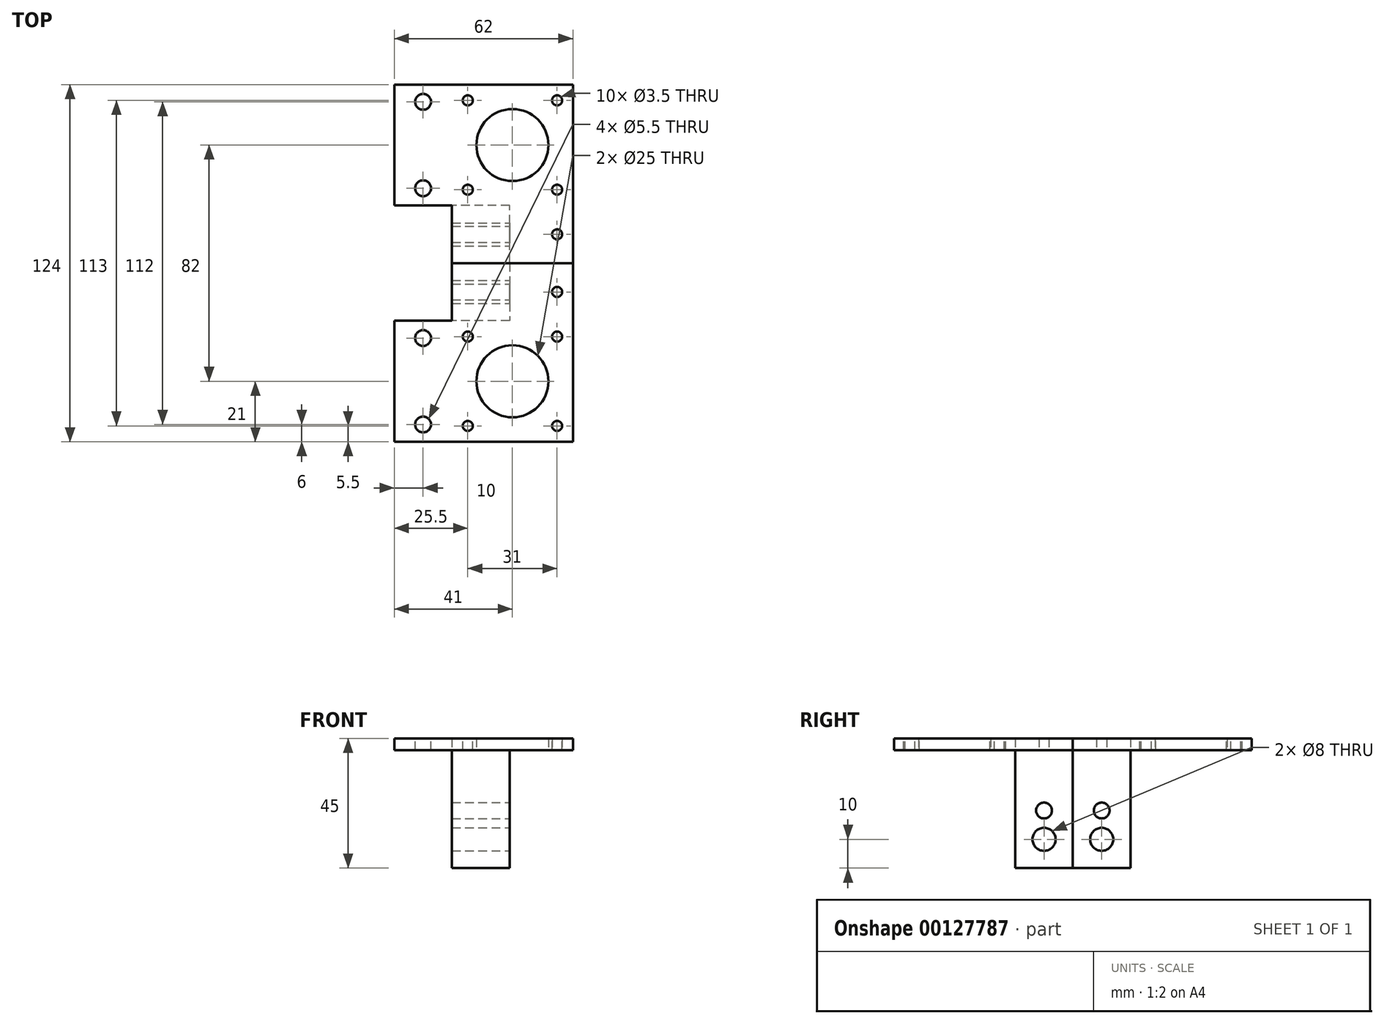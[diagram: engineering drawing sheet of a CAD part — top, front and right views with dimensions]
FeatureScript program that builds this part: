
annotation { "Feature Type Name" : "Feature", "Feature Type Description" : "" }
export const myFeature = defineFeature(function(context is Context, id is Id, definition is map)
    precondition{}
    {
        {
            var Q0;
            Q0=qCreatedBy(makeId("Top.planeOp"),FACE);
            var sketch = newSketch(context, id + "F0", { "sketchPlane" : qUnion([Q0])});
            skLineSegment(sketch, "E0.bottom", {"start": v(21, -21) * mm, "end": v(-21, -21) * mm});
            skLineSegment(sketch, "E0.top", {"start": v(21, 21) * mm, "end": v(-21, 21) * mm});
            skLineSegment(sketch, "E0.left", {"start": v(21, -21) * mm, "end": v(21, 21) * mm});
            skLineSegment(sketch, "E0.right", {"start": v(-21, -21) * mm, "end": v(-21, 21) * mm});
            skPoint(sketch, "E0.middle", {"position": v(0, 0) * mm});
            skSolve(sketch);
        }
        {
            var Q0;
            Q0=makeQuery(id+"F0.imprint","IMPRINT",FACE,{"disambiguationData":[TD([[makeQuery(id+"F0.imprint","IMPRINT",EDGE,{"derivedFrom":sQuery(id+"F0.wireOp",EDGE,"E0.bottom")}),-1.0]])]});
            extrude(context, id + "F1", {"entities" : qUnion([Q0]), "endBound" : BoundingType.SYMMETRIC, "depth" : 4 * mm});
        }
        {
            var Q0;
            Q0=makeQuery(id+"F1.opExtrude","CAP_FACE",FACE,{"disambiguationData":[OSD([sQuery(id+"F0.wireOp",EDGE,"E0.bottom"),sQuery(id+"F0.wireOp",EDGE,"E0.top"),sQuery(id+"F0.wireOp",EDGE,"E0.left"),sQuery(id+"F0.wireOp",EDGE,"E0.right")])],"isStart":false});
            var sketch = newSketch(context, id + "F2", { "sketchPlane" : qUnion([Q0])});
            skCircle(sketch, "E1", {"center": v(-15.5, 15.5) * mm, "radius": 1.75 * mm});
            skLineSegment(sketch, "E2", {"start": v(-12.66, 0) * mm, "end": v(0, 0) * mm, "construction": true});
            skLineSegment(sketch, "E3", {"start": v(0, 0) * mm, "end": v(0, 15.8) * mm, "construction": true});
            skCircle(sketch, "E4.MirrorC", {"center": v(15.5, 15.5) * mm, "radius": 1.75 * mm});
            skCircle(sketch, "E5.MirrorC", {"center": v(-15.5, -15.5) * mm, "radius": 1.75 * mm});
            skCircle(sketch, "E6.MirrorC", {"center": v(15.5, -15.5) * mm, "radius": 1.75 * mm});
            skSolve(sketch);
        }
        {
            var Q0;
            Q0=qSketchRegion(id+"F2",true);
            extrude(context, id + "F3", {"entities" : qUnion([Q0]), "operationType" : NewBodyOperationType.REMOVE, "endBound" : BoundingType.THROUGH_ALL, "oppositeDirection" : true, "depth" : 25 * mm});
        }
        {
            var Q0;
            Q0=makeQuery(id+"F1.opExtrude","SWEPT_FACE",FACE,{"disambiguationData":[OSD([sQuery(id+"F0.wireOp",EDGE,"E0.right")])]});
            extrude(context, id + "F4", {"entities" : qUnion([Q0]), "operationType" : NewBodyOperationType.ADD, "depth" : 20 * mm});
        }
        {
            var Q0;
            {var subQ0=sQuery(id+"F0.wireOp",EDGE,"E0.right");Q0=makeQuery(id+"F4.boolean.opBoolean","MERGE",FACE,{"derivedFrom":[makeQuery(id+"F1.opExtrude","CAP_FACE",FACE,{"disambiguationData":[OSD([sQuery(id+"F0.wireOp",EDGE,"E0.bottom"),sQuery(id+"F0.wireOp",EDGE,"E0.top"),sQuery(id+"F0.wireOp",EDGE,"E0.left"),subQ0])],"isStart":false}),makeQuery(id+"F4.opExtrude","SWEPT_FACE",FACE,{"disambiguationData":[OSD([subQ0]),TDD([makeQuery(id+"F1.opExtrude","CAP_EDGE",EDGE,{"disambiguationData":[OSD([subQ0])],"isStart":false})])]})]});}
            var sketch = newSketch(context, id + "F5", { "sketchPlane" : qUnion([Q0])});
            skLineSegment(sketch, "E7", {"start": v(0, 0) * mm, "end": v(-48.41, 0) * mm, "construction": true});
            skCircle(sketch, "E8", {"center": v(-31, 15) * mm, "radius": 2.75 * mm});
            skCircle(sketch, "E9.MirrorC", {"center": v(-31, -15) * mm, "radius": 2.75 * mm});
            skSolve(sketch);
        }
        {
            var Q0;
            Q0=qSketchRegion(id+"F5",true);
            extrude(context, id + "F6", {"entities" : qUnion([Q0]), "operationType" : NewBodyOperationType.REMOVE, "endBound" : BoundingType.THROUGH_ALL, "oppositeDirection" : true, "depth" : 25 * mm});
        }
        {
            var Q0;
            {var subQ0=sQuery(id+"F0.wireOp",EDGE,"E0.top");Q0=makeQuery(id+"F4.boolean.opBoolean","MERGE",FACE,{"derivedFrom":[makeQuery(id+"F1.opExtrude","SWEPT_FACE",FACE,{"disambiguationData":[OSD([subQ0])]}),makeQuery(id+"F4.opExtrude","SWEPT_FACE",FACE,{"disambiguationData":[OSD([subQ0,sQuery(id+"F0.wireOp",EDGE,"E0.right")])]})]});}
            var sketch = newSketch(context, id + "F7", { "sketchPlane" : qUnion([Q0])});
            skLineSegment(sketch, "E10.bottom", {"start": v(21, 2) * mm, "end": v(1, 2) * mm});
            skLineSegment(sketch, "E10.top", {"start": v(21, -43) * mm, "end": v(1, -43) * mm});
            skLineSegment(sketch, "E10.left", {"start": v(21, 2) * mm, "end": v(21, -43) * mm});
            skLineSegment(sketch, "E10.right", {"start": v(1, 2) * mm, "end": v(1, -43) * mm});
            skSolve(sketch);
        }
        {
            var Q0;
            Q0=qSketchRegion(id+"F7",true);
            extrude(context, id + "F8", {"entities" : qUnion([Q0]), "operationType" : NewBodyOperationType.ADD, "depth" : 20 * mm});
        }
        {
            var Q0;
            {var subQ0=sQuery(id+"F0.wireOp",EDGE,"E0.left");var subQ1=sQuery(id+"F0.wireOp",EDGE,"E0.right");var subQ2=sQuery(id+"F0.wireOp",EDGE,"E0.top");Q0=makeQuery(id+"F8.boolean.opBoolean","SPLIT",FACE,{"disambiguationData":[TD([makeQuery(id+"F1.opExtrude","SWEPT_FACE",FACE,{"disambiguationData":[OSD([subQ0])]})])],"derivedFrom":makeQuery(id+"F4.boolean.opBoolean","MERGE",FACE,{"derivedFrom":[makeQuery(id+"F1.opExtrude","SWEPT_FACE",FACE,{"disambiguationData":[OSD([subQ2])]}),makeQuery(id+"F4.opExtrude","SWEPT_FACE",FACE,{"disambiguationData":[OSD([subQ2,subQ1])]})]})});}
            var Q1;
            Q1=makeQuery(id+"F8.opExtrude","CAP_FACE",FACE,{"disambiguationData":[OSD([sQuery(id+"F7.wireOp",EDGE,"E10.bottom"),sQuery(id+"F7.wireOp",EDGE,"E10.top"),sQuery(id+"F7.wireOp",EDGE,"E10.left"),sQuery(id+"F7.wireOp",EDGE,"E10.right")])],"isStart":false});
            extrude(context, id + "F9", {"entities" : qUnion([Q0]), "operationType" : NewBodyOperationType.ADD, "endBound" : BoundingType.UP_TO_SURFACE, "endBoundEntityFace" : qUnion([Q1]), "depth" : 25 * mm});
        }
        {
            var Q0;
            Q0=makeQuery(id+"F8.opExtrude","SWEPT_FACE",FACE,{"disambiguationData":[OSD([sQuery(id+"F7.wireOp",EDGE,"E10.right")])]});
            var sketch = newSketch(context, id + "F10", { "sketchPlane" : qUnion([Q0])});
            skCircle(sketch, "E11", {"center": v(31, -33) * mm, "radius": 4 * mm});
            skLineSegment(sketch, "E12", {"start": v(31, -33) * mm, "end": v(31, -43) * mm, "construction": true});
            skCircle(sketch, "E13", {"center": v(31, -23) * mm, "radius": 2.75 * mm});
            skSolve(sketch);
        }
        {
            var Q0;
            Q0=qSketchRegion(id+"F10",true);
            extrude(context, id + "F11", {"entities" : qUnion([Q0]), "operationType" : NewBodyOperationType.REMOVE, "endBound" : BoundingType.THROUGH_ALL, "oppositeDirection" : true, "depth" : 25 * mm});
        }
        {
            var Q0;
            {var subQ0=sQuery(id+"F0.wireOp",EDGE,"E0.right");var subQ1=sQuery(id+"F0.wireOp",EDGE,"E0.top");var subQ2=sQuery(id+"F0.wireOp",EDGE,"E0.left");var subQ3=makeQuery(id+"F1.opExtrude","CAP_FACE",FACE,{"disambiguationData":[OSD([sQuery(id+"F0.wireOp",EDGE,"E0.bottom"),subQ1,subQ2,subQ0])],"isStart":true});var subQ4=sQuery(id+"F7.wireOp",EDGE,"E10.right");var subQ5=makeQuery(id+"F4.opExtrude","SWEPT_FACE",FACE,{"disambiguationData":[OSD([subQ0]),TDD([makeQuery(id+"F1.opExtrude","CAP_EDGE",EDGE,{"disambiguationData":[OSD([subQ0])],"isStart":true})])]});Q0=makeQuery(id+"F9.boolean.opBoolean","MERGE",FACE,{"derivedFrom":[makeQuery(id+"F4.boolean.opBoolean","MERGE",FACE,{"derivedFrom":[subQ3,subQ5]}),makeQuery(id+"F9.opExtrude","SWEPT_FACE",FACE,{"disambiguationData":[OSD([subQ1,subQ0]),TDD([makeQuery(id+"F8.boolean.opBoolean","SPLIT",EDGE,{"disambiguationData":[TD([subQ3,makeQuery(id+"F1.opExtrude","SWEPT_FACE",FACE,{"disambiguationData":[OSD([subQ1])]}),makeQuery(id+"F1.opExtrude","SWEPT_FACE",FACE,{"disambiguationData":[OSD([subQ2])]}),makeQuery(id+"F4.opExtrude","SWEPT_FACE",FACE,{"disambiguationData":[OSD([subQ1,subQ0])]}),subQ5,makeQuery(id+"F8.opExtrude","CAP_FACE",FACE,{"disambiguationData":[OSD([sQuery(id+"F7.wireOp",EDGE,"E10.bottom"),sQuery(id+"F7.wireOp",EDGE,"E10.top"),sQuery(id+"F7.wireOp",EDGE,"E10.left"),subQ4])],"isStart":true}),makeQuery(id+"F8.opExtrude","SWEPT_FACE",FACE,{"disambiguationData":[OSD([subQ4])]})])],"derivedFrom":makeQuery(id+"F4.boolean.opBoolean","MERGE",EDGE,{"derivedFrom":[makeQuery(id+"F1.opExtrude","CAP_EDGE",EDGE,{"disambiguationData":[OSD([subQ1])],"isStart":true}),makeQuery(id+"F4.opExtrude","SWEPT_EDGE",EDGE,{"disambiguationData":[OSD([subQ1,subQ0]),TDD([makeQuery(id+"F1.opExtrude","CAP_VERTEX",VERTEX,{"disambiguationData":[OSD([subQ1,subQ0])],"isStart":true})])]})]})})])]})]});}
            var sketch = newSketch(context, id + "F12", { "sketchPlane" : qUnion([Q0])});
            skCircle(sketch, "E14", {"center": v(15.5, -31) * mm, "radius": 1.75 * mm});
            skCircle(sketch, "E15.0", {"center": v(15.5, -15.5) * mm, "radius": 1.75 * mm, "construction": true});
            skLineSegment(sketch, "E16", {"start": v(15.5, -31) * mm, "end": v(-1, -31) * mm, "construction": true});
            skSolve(sketch);
        }
        {
            var Q0;
            Q0=qSketchRegion(id+"F12",true);
            extrude(context, id + "F13", {"entities" : qUnion([Q0]), "operationType" : NewBodyOperationType.REMOVE, "endBound" : BoundingType.THROUGH_ALL, "oppositeDirection" : true, "depth" : 25 * mm});
        }
        {
            var Q0;
            {var subQ0=sQuery(id+"F0.wireOp",EDGE,"E0.right");var subQ1=sQuery(id+"F0.wireOp",EDGE,"E0.top");var subQ2=sQuery(id+"F0.wireOp",EDGE,"E0.left");var subQ3=makeQuery(id+"F1.opExtrude","CAP_FACE",FACE,{"disambiguationData":[OSD([sQuery(id+"F0.wireOp",EDGE,"E0.bottom"),subQ1,subQ2,subQ0])],"isStart":true});var subQ4=sQuery(id+"F7.wireOp",EDGE,"E10.right");var subQ5=makeQuery(id+"F4.opExtrude","SWEPT_FACE",FACE,{"disambiguationData":[OSD([subQ0]),TDD([makeQuery(id+"F1.opExtrude","CAP_EDGE",EDGE,{"disambiguationData":[OSD([subQ0])],"isStart":true})])]});Q0=makeQuery(id+"F9.boolean.opBoolean","MERGE",FACE,{"derivedFrom":[makeQuery(id+"F4.boolean.opBoolean","MERGE",FACE,{"derivedFrom":[subQ3,subQ5]}),makeQuery(id+"F9.opExtrude","SWEPT_FACE",FACE,{"disambiguationData":[OSD([subQ1,subQ0]),TDD([makeQuery(id+"F8.boolean.opBoolean","SPLIT",EDGE,{"disambiguationData":[TD([subQ3,makeQuery(id+"F1.opExtrude","SWEPT_FACE",FACE,{"disambiguationData":[OSD([subQ1])]}),makeQuery(id+"F1.opExtrude","SWEPT_FACE",FACE,{"disambiguationData":[OSD([subQ2])]}),makeQuery(id+"F4.opExtrude","SWEPT_FACE",FACE,{"disambiguationData":[OSD([subQ1,subQ0])]}),subQ5,makeQuery(id+"F8.opExtrude","CAP_FACE",FACE,{"disambiguationData":[OSD([sQuery(id+"F7.wireOp",EDGE,"E10.bottom"),sQuery(id+"F7.wireOp",EDGE,"E10.top"),sQuery(id+"F7.wireOp",EDGE,"E10.left"),subQ4])],"isStart":true}),makeQuery(id+"F8.opExtrude","SWEPT_FACE",FACE,{"disambiguationData":[OSD([subQ4])]})])],"derivedFrom":makeQuery(id+"F4.boolean.opBoolean","MERGE",EDGE,{"derivedFrom":[makeQuery(id+"F1.opExtrude","CAP_EDGE",EDGE,{"disambiguationData":[OSD([subQ1])],"isStart":true}),makeQuery(id+"F4.opExtrude","SWEPT_EDGE",EDGE,{"disambiguationData":[OSD([subQ1,subQ0]),TDD([makeQuery(id+"F1.opExtrude","CAP_VERTEX",VERTEX,{"disambiguationData":[OSD([subQ1,subQ0])],"isStart":true})])]})]})})])]})]});}
            var sketch = newSketch(context, id + "F14", { "sketchPlane" : qUnion([Q0])});
            skCircle(sketch, "E17", {"center": v(0, 0) * mm, "radius": 12.5 * mm});
            skSolve(sketch);
        }
        {
            var Q0;
            Q0=qSketchRegion(id+"F14",true);
            extrude(context, id + "F15", {"entities" : qUnion([Q0]), "operationType" : NewBodyOperationType.REMOVE, "endBound" : BoundingType.THROUGH_ALL, "oppositeDirection" : true, "depth" : 25 * mm});
        }
        {
            var Q0;
            Q0=makeQuery(id+"F1.opExtrude","SWEPT_BODY",BODY,{"disambiguationData":[OSD([sQuery(id+"F0.wireOp",EDGE,"E0.bottom"),sQuery(id+"F0.wireOp",EDGE,"E0.top"),sQuery(id+"F0.wireOp",EDGE,"E0.left"),sQuery(id+"F0.wireOp",EDGE,"E0.right")])]});
            var Q1;
            {var subQ0=sQuery(id+"F7.wireOp",EDGE,"E10.right");var subQ1=sQuery(id+"F7.wireOp",EDGE,"E10.left");var subQ2=sQuery(id+"F7.wireOp",EDGE,"E10.top");var subQ3=sQuery(id+"F7.wireOp",EDGE,"E10.bottom");Q1=makeQuery(id+"F9.boolean.opBoolean","MERGE",FACE,{"derivedFrom":[makeQuery(id+"F8.opExtrude","CAP_FACE",FACE,{"disambiguationData":[OSD([subQ3,subQ2,subQ1,subQ0])],"isStart":false}),makeQuery(id+"F9.opExtrude","CAP_FACE",FACE,{"disambiguationData":[OSD([subQ3,subQ2,subQ1,subQ0])],"isStart":false})]});}
            mirror(context, id + "F16", {"entities" : qUnion([Q0]), "mirrorPlane" : qUnion([Q1])});
        }
    });
